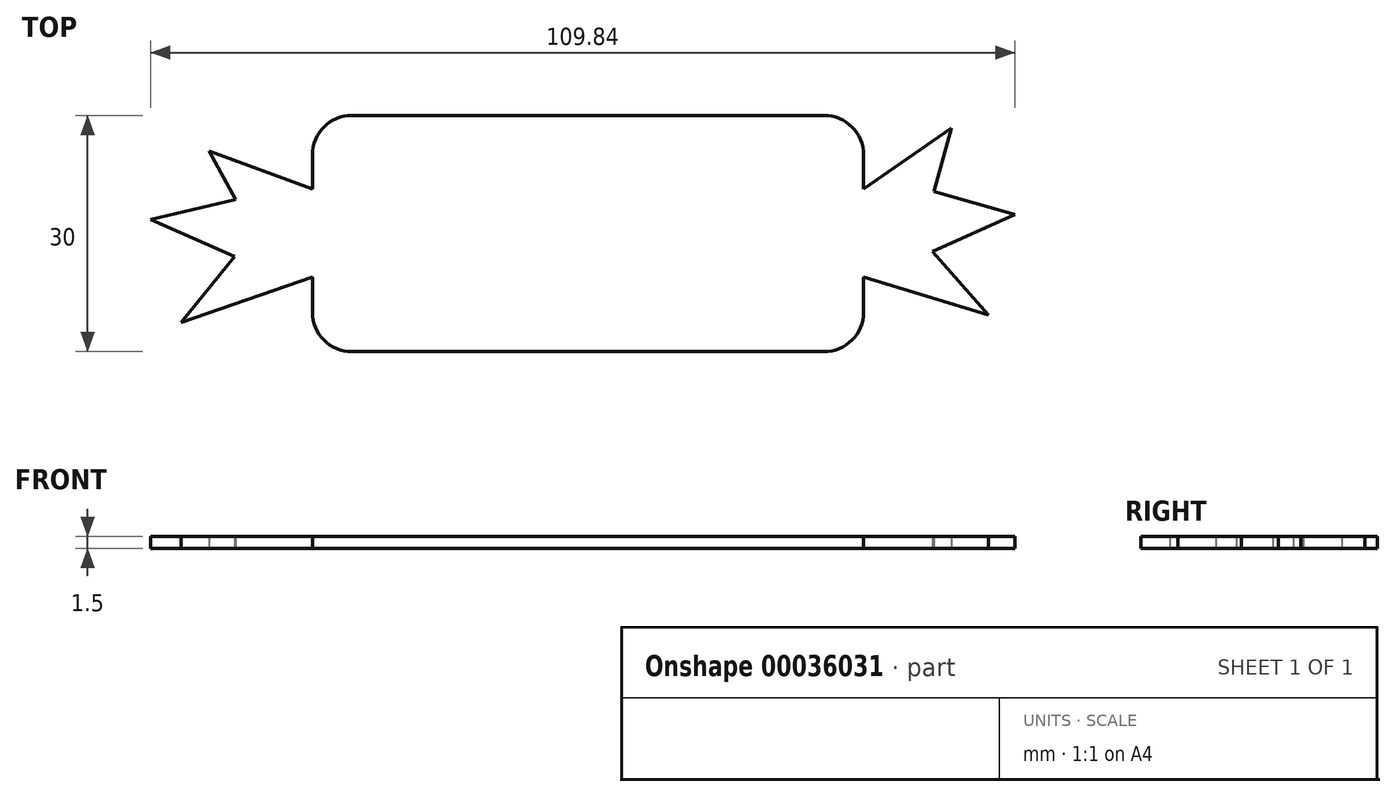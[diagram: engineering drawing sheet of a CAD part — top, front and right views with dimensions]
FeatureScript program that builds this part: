
annotation { "Feature Type Name" : "Feature", "Feature Type Description" : "" }
export const myFeature = defineFeature(function(context is Context, id is Id, definition is map)
    precondition{}
    {
        {
            var Q0;
            Q0=qCreatedBy(makeId("Top.planeOp"),FACE);
            var sketch = newSketch(context, id + "F0", { "sketchPlane" : qUnion([Q0])});
            skLineSegment(sketch, "E0.rect.bottom", {"start": v(-30, 15) * mm, "end": v(30, 15) * mm});
            skLineSegment(sketch, "E0.rect.top", {"start": v(-30, -15) * mm, "end": v(30, -15) * mm});
            skLineSegment(sketch, "E0.rect.left", {"start": v(-35, 10) * mm, "end": v(-35, -10) * mm});
            skLineSegment(sketch, "E0.rect.right", {"start": v(35, 10) * mm, "end": v(35, -10) * mm});
            skPoint(sketch, "E0.rect.middle", {"position": v(0, 0) * mm});
            skPoint(sketch, "E1.visualSharp", {"position": v(-35, 15) * mm});
            skArc(sketch, "E1.filletArc", {"start": v(-30, 15) * mm, "mid": v(-33.54, 13.54) * mm, "end": v(-35, 10) * mm});
            skPoint(sketch, "E2.visualSharp", {"position": v(35, 15) * mm});
            skArc(sketch, "E2.filletArc", {"start": v(35, 10) * mm, "mid": v(33.54, 13.54) * mm, "end": v(30, 15) * mm});
            skPoint(sketch, "E3.visualSharp", {"position": v(35, -15) * mm});
            skArc(sketch, "E3.filletArc", {"start": v(30, -15) * mm, "mid": v(33.54, -13.54) * mm, "end": v(35, -10) * mm});
            skPoint(sketch, "E4.visualSharp", {"position": v(-35, -15) * mm});
            skArc(sketch, "E4.filletArc", {"start": v(-35, -10) * mm, "mid": v(-33.54, -13.54) * mm, "end": v(-30, -15) * mm});
            skPoint(sketch, "E5", {"position": v(-35, 0) * mm});
            skPoint(sketch, "E6", {"position": v(35, 0) * mm});
            skLineSegment(sketch, "E7", {"start": v(-35, 5.64) * mm, "end": v(-48.15, 10.49) * mm});
            skLineSegment(sketch, "E8", {"start": v(-48.15, 10.49) * mm, "end": v(-44.75, 4.35) * mm});
            skLineSegment(sketch, "E9", {"start": v(-44.75, 4.35) * mm, "end": v(-55.58, 1.76) * mm});
            skLineSegment(sketch, "E10", {"start": v(-55.58, 1.76) * mm, "end": v(-44.92, -2.92) * mm});
            skLineSegment(sketch, "E11", {"start": v(-44.92, -2.92) * mm, "end": v(-51.7, -11.33) * mm});
            skLineSegment(sketch, "E12", {"start": v(-51.7, -11.33) * mm, "end": v(-35, -5.5) * mm});
            skLineSegment(sketch, "E13", {"start": v(-35, -5.5) * mm, "end": v(-35, 5.64) * mm});
            skLineSegment(sketch, "E14", {"start": v(35, 5.64) * mm, "end": v(46.2, 13.4) * mm});
            skLineSegment(sketch, "E15", {"start": v(46.2, 13.4) * mm, "end": v(43.93, 5.32) * mm});
            skLineSegment(sketch, "E16", {"start": v(43.93, 5.32) * mm, "end": v(54.26, 2.42) * mm});
            skLineSegment(sketch, "E17", {"start": v(54.26, 2.42) * mm, "end": v(43.77, -2.28) * mm});
            skLineSegment(sketch, "E18", {"start": v(43.77, -2.28) * mm, "end": v(50.88, -10.36) * mm});
            skLineSegment(sketch, "E19", {"start": v(50.88, -10.36) * mm, "end": v(35, -5.5) * mm});
            skLineSegment(sketch, "E20", {"start": v(35, -5.5) * mm, "end": v(35, 5.64) * mm});
            skSolve(sketch);
        }
        {
            var Q0;
            Q0 = qSketchRegion(id + "F0", true);
            extrude(context, id + "F1", {"entities" : qUnion([Q0]), "depth" : 1.5 * mm});
        }
    });
